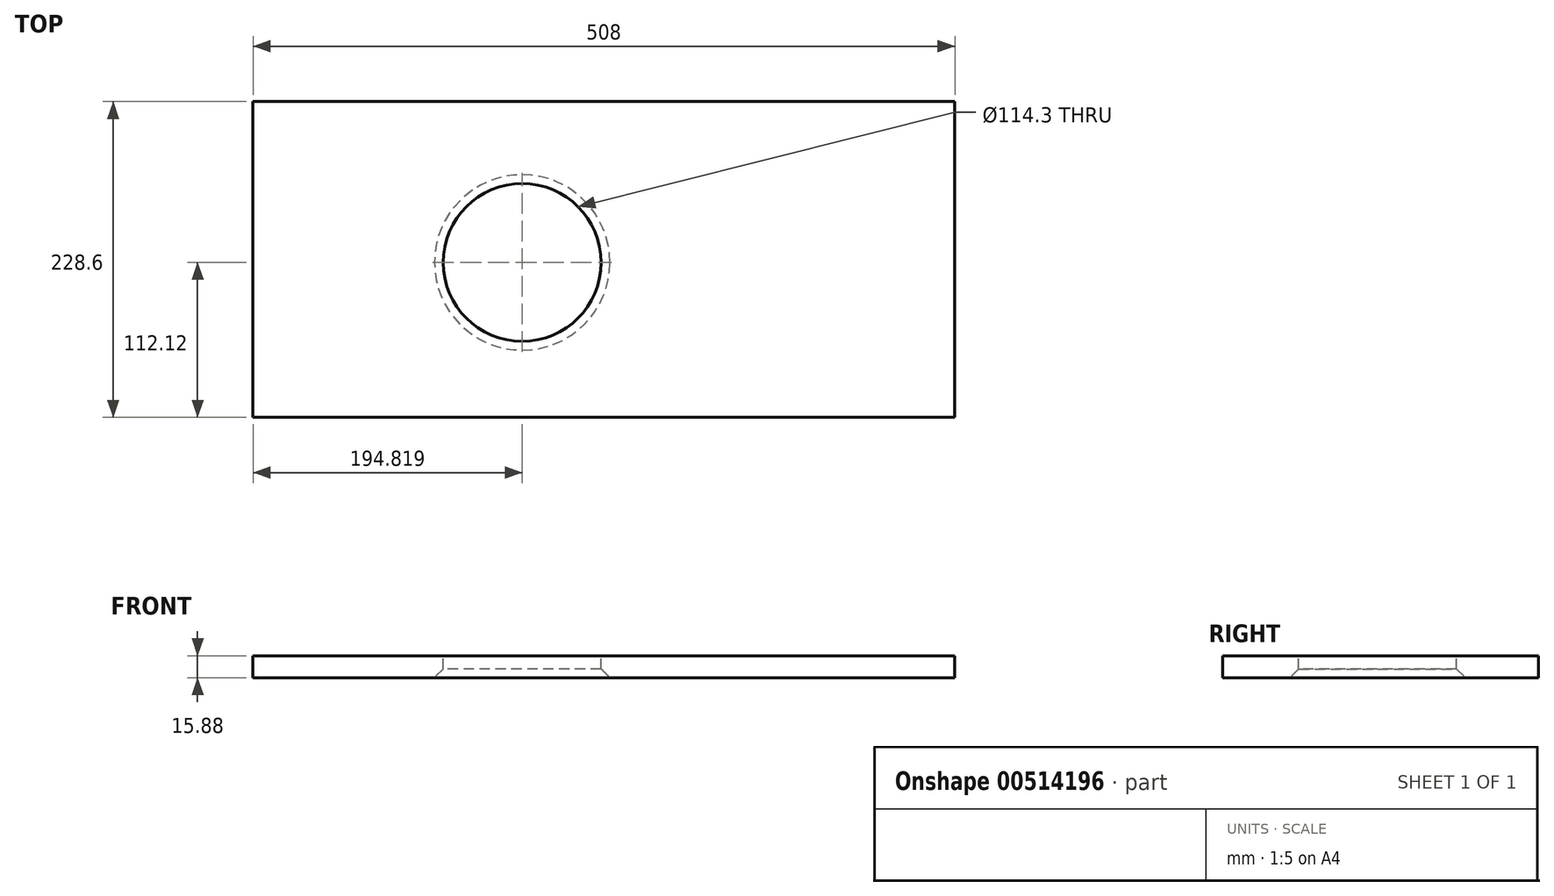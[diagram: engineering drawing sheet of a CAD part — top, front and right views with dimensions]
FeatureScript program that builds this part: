
annotation { "Feature Type Name" : "Feature", "Feature Type Description" : "" }
export const myFeature = defineFeature(function(context is Context, id is Id, definition is map)
    precondition{}
    {
        {
            var Q0;
            Q0=qCreatedBy(makeId("Top.planeOp"),FACE);
            var sketch = newSketch(context, id + "F0", { "sketchPlane" : qUnion([Q0])});
            skLineSegment(sketch, "E0.bottom", {"start": v(254.58, 116.48) * mm, "end": v(-253.42, 116.48) * mm});
            skLineSegment(sketch, "E0.top", {"start": v(254.58, -112.12) * mm, "end": v(-253.42, -112.12) * mm});
            skLineSegment(sketch, "E0.left", {"start": v(254.58, 116.48) * mm, "end": v(254.58, -112.12) * mm});
            skLineSegment(sketch, "E0.right", {"start": v(-253.42, 116.48) * mm, "end": v(-253.42, -112.12) * mm});
            skSolve(sketch);
        }
        {
            var Q0;
            Q0 = qSketchRegion(id + "F0", true);
            extrude(context, id + "F1", {"entities" : qUnion([Q0]), "depth" : 15.88 * mm});
        }
        {
            var Q0;
            Q0=makeQuery(id+"F1.opExtrude","SWEPT_FACE",FACE,{"disambiguationData":[OSD([sQuery(id+"F0.wireOp",EDGE,"E0.left")])]});
            var sketch = newSketch(context, id + "F2", { "sketchPlane" : qUnion([Q0])});
            skLineSegment(sketch, "E1.bottom", {"start": v(-112.12, 15.88) * mm, "end": v(116.48, 15.88) * mm});
            skLineSegment(sketch, "E1.top", {"start": v(-112.12, 117.48) * mm, "end": v(116.48, 117.48) * mm});
            skLineSegment(sketch, "E1.left", {"start": v(-112.12, 15.88) * mm, "end": v(-112.12, 117.48) * mm});
            skLineSegment(sketch, "E1.right", {"start": v(116.48, 15.88) * mm, "end": v(116.48, 117.48) * mm});
            skSolve(sketch);
        }
        {
            var Q0;
            Q0 = qSketchRegion(id + "F2", true);
            extrude(context, id + "F3", {"entities" : qUnion([Q0]), "depth" : 25.4 * mm});
        }
        {
            var Q0;
            Q0=makeQuery(id+"F3.opExtrude","SWEPT_BODY",BODY,{"disambiguationData":[OSD([sQuery(id+"F2.wireOp",EDGE,"E1.bottom"),sQuery(id+"F2.wireOp",EDGE,"E1.top"),sQuery(id+"F2.wireOp",EDGE,"E1.left"),sQuery(id+"F2.wireOp",EDGE,"E1.right")])]});
            deleteBodies(context, id + "F4", {"entities" : qUnion([Q0])});
        }
        {
            var Q0;
            Q0=qCreatedBy(makeId("Top.planeOp"),FACE);
            var sketch = newSketch(context, id + "F5", { "sketchPlane" : qUnion([Q0]), "disableImprinting" : false});
            skCircle(sketch, "E2", {"center": v(-58.6, 0) * mm, "radius": 63.5 * mm});
            skSolve(sketch);
        }
        {
            var Q0;
            Q0=sQuery(id+"F5.wireOp",VERTEX,"E2.center");
            var Q1;
            Q1=makeQuery(id+"F1.opExtrude","SWEPT_BODY",BODY,{"disambiguationData":[OSD([sQuery(id+"F0.wireOp",EDGE,"E0.bottom"),sQuery(id+"F0.wireOp",EDGE,"E0.top"),sQuery(id+"F0.wireOp",EDGE,"E0.left"),sQuery(id+"F0.wireOp",EDGE,"E0.right")])]});
            hole(context, id + "F6", {"style" : HoleStyle.C_SINK, "endStyle" : HoleEndStyle.THROUGH, "oppositeDirection" : true, "holeDiameter" : 114.3 * mm, "cSinkDiameter" : 127 * mm, "cSinkAngle" : 90 * degree, "isTappedThrough" : true, "tappedDepth" : 12.7 * mm, "tapClearance" : 3, "locations" : qUnion([Q0]), "scope" : qUnion([Q1])});
        }
    });
